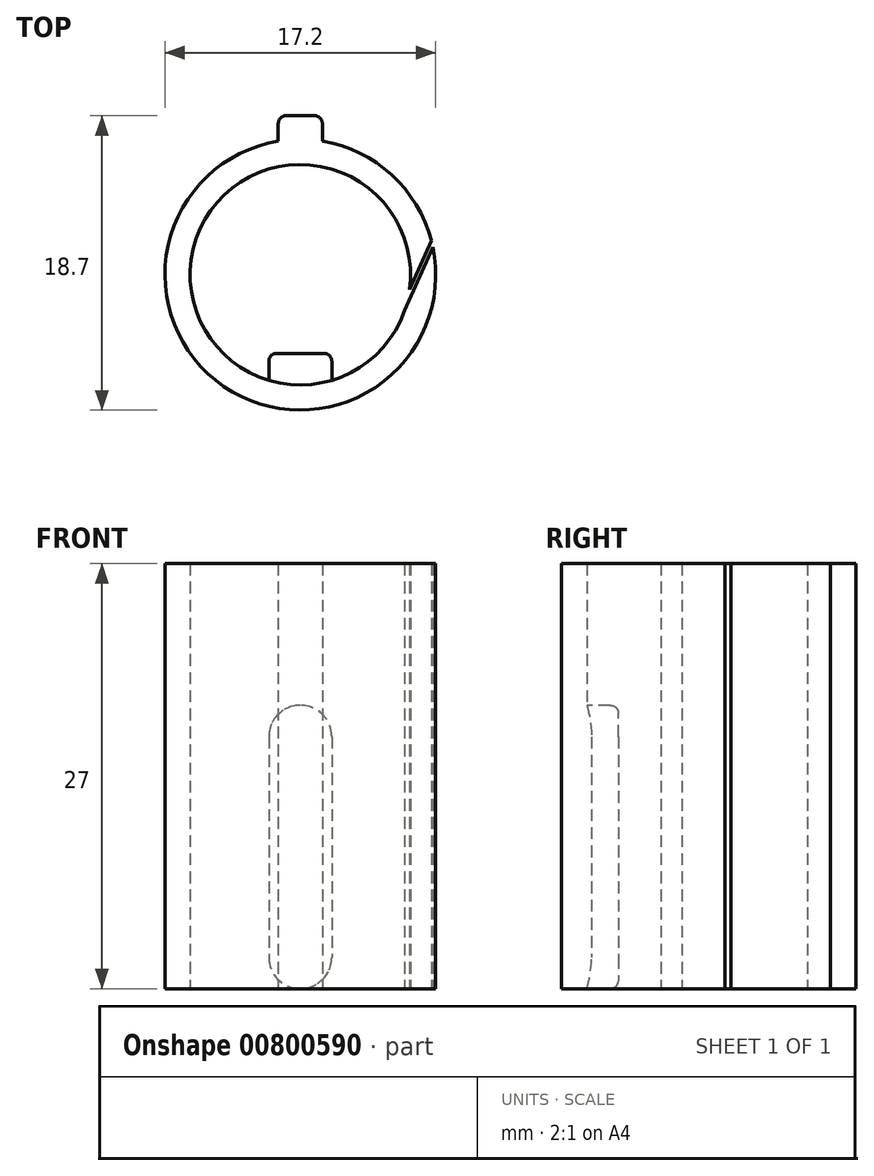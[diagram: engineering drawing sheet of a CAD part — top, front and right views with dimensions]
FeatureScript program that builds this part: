
annotation { "Feature Type Name" : "Feature", "Feature Type Description" : "" }
export const myFeature = defineFeature(function(context is Context, id is Id, definition is map)
    precondition{}
    {
        {
            var Q0;
            Q0=qCreatedBy(makeId("Top.planeOp"),FACE);
            var sketch = newSketch(context, id + "F0", { "sketchPlane" : qUnion([Q0])});
            skArc(sketch, "E0", {"start": v(2, -6.7) * mm, "mid": v(4.84, -5.06) * mm, "end": v(6.62, -2.29) * mm});
            skArc(sketch, "E1", {"start": v(-1.4, 8.49) * mm, "mid": v(-4.86, -7.1) * mm, "end": v(8.42, 1.76) * mm});
            skLineSegment(sketch, "E2.top", {"start": v(-1.4, 10.1) * mm, "end": v(1.4, 10.1) * mm});
            skLineSegment(sketch, "E2.left", {"start": v(-1.4, 8.49) * mm, "end": v(-1.4, 10.1) * mm});
            skLineSegment(sketch, "E2.right", {"start": v(1.4, 8.49) * mm, "end": v(1.4, 10.1) * mm});
            skLineSegment(sketch, "E3.top", {"start": v(-2, -5) * mm, "end": v(2, -5) * mm});
            skLineSegment(sketch, "E3.left", {"start": v(-2, -6.7) * mm, "end": v(-2, -5) * mm});
            skLineSegment(sketch, "E3.right", {"start": v(2, -6.7) * mm, "end": v(2, -5) * mm});
            skLineSegment(sketch, "E4", {"start": v(6.62, -2.29) * mm, "end": v(8.42, 1.76) * mm});
            skLineSegment(sketch, "E5", {"start": v(6.93, -0.96) * mm, "end": v(8.32, 2.16) * mm});
            skArc(sketch, "E6.trimOffspring", {"start": v(8.32, 2.16) * mm, "mid": v(5.8, 6.35) * mm, "end": v(1.4, 8.49) * mm});
            skArc(sketch, "E7.trimOffspring", {"start": v(6.93, -0.96) * mm, "mid": v(-3.79, 5.89) * mm, "end": v(-2, -6.7) * mm});
            skArc(sketch, "E8", {"start": v(6.93, -0.96) * mm, "mid": v(-6.8, 1.63) * mm, "end": v(6.62, -2.29) * mm});
            skSolve(sketch);
        }
        {
            var Q0;
            Q0=makeQuery(id+"F0.imprint","IMPRINT",FACE,{"disambiguationData":[TD([[makeQuery(id+"F0.imprint","IMPRINT",EDGE,{"derivedFrom":sQuery(id+"F0.wireOp",EDGE,"E1")}),1.0]])]});
            extrude(context, id + "F1", {"entities" : qUnion([Q0]), "depth" : 27 * mm, "offsetDistance" : 25 * mm});
        }
        {
            var Q0;
            Q0 = qSketchRegion(id + "F0", true);
            extrude(context, id + "F2", {"entities" : qUnion([Q0]), "operationType" : NewBodyOperationType.ADD, "depth" : 18 * mm, "offsetDistance" : 25 * mm});
        }
        {
            var Q0;
            Q0=makeQuery(id+"F2.opExtrude","CAP_EDGE",EDGE,{"disambiguationData":[OSD([sQuery(id+"F0.wireOp",EDGE,"E3.right")])],"isStart":false});
            var Q1;
            Q1=makeQuery(id+"F2.opExtrude","CAP_EDGE",EDGE,{"disambiguationData":[OSD([sQuery(id+"F0.wireOp",EDGE,"E3.left")])],"isStart":false});
            var Q2;
            Q2=makeQuery(id+"F2.opExtrude","CAP_EDGE",EDGE,{"disambiguationData":[OSD([sQuery(id+"F0.wireOp",EDGE,"E3.right")])],"isStart":true});
            var Q3;
            Q3=makeQuery(id+"F2.opExtrude","CAP_EDGE",EDGE,{"disambiguationData":[OSD([sQuery(id+"F0.wireOp",EDGE,"E3.left")])],"isStart":true});
            fillet(context, id + "F3", {"entities" : qUnion([Q0, Q1, Q2, Q3]), "radius" : 2 * mm, "tangentPropagation" : true, "allowEdgeOverflow" : false});
        }
        {
            var Q0;
            Q0=makeQuery(id+"F2.opExtrude","SWEPT_EDGE",EDGE,{"disambiguationData":[OSD([sQuery(id+"F0.wireOp",EDGE,"E3.top"),sQuery(id+"F0.wireOp",EDGE,"E3.right")])]});
            var Q1;
            Q1=makeQuery(id+"F1.opExtrude","SWEPT_EDGE",EDGE,{"disambiguationData":[OSD([sQuery(id+"F0.wireOp",EDGE,"E2.top"),sQuery(id+"F0.wireOp",EDGE,"E2.right")])]});
            var Q2;
            Q2=makeQuery(id+"F1.opExtrude","SWEPT_EDGE",EDGE,{"disambiguationData":[OSD([sQuery(id+"F0.wireOp",EDGE,"E2.top"),sQuery(id+"F0.wireOp",EDGE,"E2.left")])]});
            fillet(context, id + "F4", {"entities" : qUnion([Q0, Q1, Q2]), "radius" : 0.5 * mm, "tangentPropagation" : true, "allowEdgeOverflow" : false});
        }
    });
